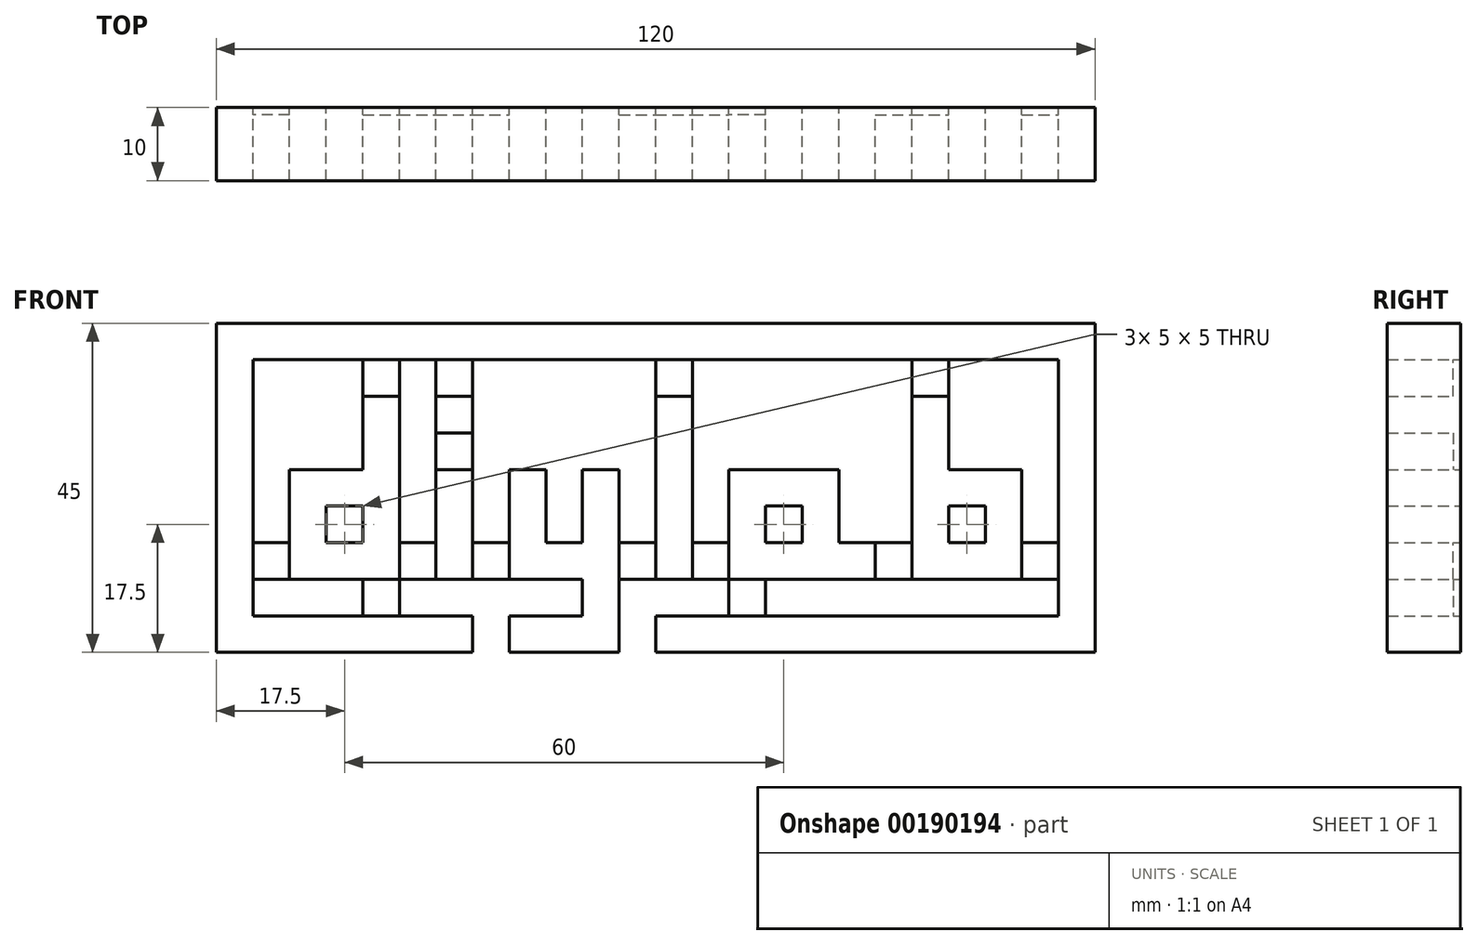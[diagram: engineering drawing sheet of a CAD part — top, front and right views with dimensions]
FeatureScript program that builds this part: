
annotation { "Feature Type Name" : "Feature", "Feature Type Description" : "" }
export const myFeature = defineFeature(function(context is Context, id is Id, definition is map)
    precondition{}
    {
        {
            var Q0;
            Q0=qCreatedBy(makeId("Front.planeOp"),FACE);
            var sketch = newSketch(context, id + "F0", { "sketchPlane" : qUnion([Q0])});
            skLineSegment(sketch, "E0", {"start": v(35, 0) * mm, "end": v(35, 5) * mm});
            skLineSegment(sketch, "E1", {"start": v(35, 5) * mm, "end": v(5, 5) * mm});
            skLineSegment(sketch, "E2", {"start": v(5, 5) * mm, "end": v(5, 40) * mm});
            skLineSegment(sketch, "E3", {"start": v(5, 40) * mm, "end": v(115, 40) * mm});
            skLineSegment(sketch, "E4", {"start": v(115, 40) * mm, "end": v(115, 5) * mm});
            skLineSegment(sketch, "E5", {"start": v(115, 5) * mm, "end": v(60, 5) * mm});
            skLineSegment(sketch, "E6", {"start": v(60, 5) * mm, "end": v(60, 0) * mm});
            skLineSegment(sketch, "E7", {"start": v(60, 0) * mm, "end": v(120, 0) * mm});
            skLineSegment(sketch, "E8", {"start": v(120, 0) * mm, "end": v(120, 45) * mm});
            skLineSegment(sketch, "E9", {"start": v(120, 45) * mm, "end": v(0, 45) * mm});
            skLineSegment(sketch, "E10", {"start": v(0, 45) * mm, "end": v(0, 0) * mm});
            skLineSegment(sketch, "E11", {"start": v(0, 0) * mm, "end": v(35, 0) * mm});
            skLineSegment(sketch, "E12", {"start": v(10, 25) * mm, "end": v(10, 10) * mm});
            skLineSegment(sketch, "E13", {"start": v(10, 10) * mm, "end": v(25, 10) * mm});
            skLineSegment(sketch, "E14", {"start": v(25, 10) * mm, "end": v(25, 35) * mm});
            skLineSegment(sketch, "E15", {"start": v(25, 35) * mm, "end": v(20, 35) * mm});
            skLineSegment(sketch, "E16", {"start": v(20, 35) * mm, "end": v(20, 25) * mm});
            skLineSegment(sketch, "E17", {"start": v(20, 25) * mm, "end": v(10, 25) * mm});
            skLineSegment(sketch, "E18", {"start": v(30, 25) * mm, "end": v(30, 10) * mm});
            skLineSegment(sketch, "E19", {"start": v(30, 10) * mm, "end": v(35, 10) * mm});
            skLineSegment(sketch, "E20", {"start": v(35, 10) * mm, "end": v(35, 25) * mm});
            skLineSegment(sketch, "E21", {"start": v(35, 25) * mm, "end": v(30, 25) * mm});
            skLineSegment(sketch, "E22", {"start": v(40, 5) * mm, "end": v(40, 0) * mm});
            skLineSegment(sketch, "E23", {"start": v(40, 0) * mm, "end": v(55, 0) * mm});
            skLineSegment(sketch, "E24", {"start": v(55, 0) * mm, "end": v(55, 25) * mm});
            skLineSegment(sketch, "E25", {"start": v(55, 25) * mm, "end": v(50, 25) * mm});
            skLineSegment(sketch, "E26", {"start": v(50, 25) * mm, "end": v(50, 15) * mm});
            skLineSegment(sketch, "E27", {"start": v(50, 15) * mm, "end": v(45, 15) * mm});
            skLineSegment(sketch, "E28", {"start": v(45, 15) * mm, "end": v(45, 25) * mm});
            skLineSegment(sketch, "E29", {"start": v(45, 25) * mm, "end": v(40, 25) * mm});
            skLineSegment(sketch, "E30", {"start": v(40, 25) * mm, "end": v(40, 10) * mm});
            skLineSegment(sketch, "E31", {"start": v(40, 10) * mm, "end": v(50, 10) * mm});
            skLineSegment(sketch, "E32", {"start": v(50, 10) * mm, "end": v(50, 5) * mm});
            skLineSegment(sketch, "E33", {"start": v(50, 5) * mm, "end": v(40, 5) * mm});
            skLineSegment(sketch, "E34", {"start": v(20, 15) * mm, "end": v(15, 15) * mm});
            skLineSegment(sketch, "E35", {"start": v(15, 15) * mm, "end": v(15, 20) * mm});
            skLineSegment(sketch, "E36", {"start": v(15, 20) * mm, "end": v(20, 20) * mm});
            skLineSegment(sketch, "E37", {"start": v(20, 20) * mm, "end": v(20, 15) * mm});
            skLineSegment(sketch, "E38", {"start": v(60, 35) * mm, "end": v(60, 10) * mm});
            skLineSegment(sketch, "E39", {"start": v(60, 10) * mm, "end": v(65, 10) * mm});
            skLineSegment(sketch, "E40", {"start": v(65, 10) * mm, "end": v(65, 35) * mm});
            skLineSegment(sketch, "E41", {"start": v(65, 35) * mm, "end": v(60, 35) * mm});
            skLineSegment(sketch, "E42", {"start": v(70, 10) * mm, "end": v(90, 10) * mm});
            skLineSegment(sketch, "E43", {"start": v(90, 10) * mm, "end": v(90, 15) * mm});
            skLineSegment(sketch, "E44", {"start": v(90, 15) * mm, "end": v(85, 15) * mm});
            skLineSegment(sketch, "E45", {"start": v(85, 15) * mm, "end": v(85, 25) * mm});
            skLineSegment(sketch, "E46", {"start": v(85, 25) * mm, "end": v(70, 25) * mm});
            skLineSegment(sketch, "E47", {"start": v(70, 25) * mm, "end": v(70, 10) * mm});
            skLineSegment(sketch, "E48", {"start": v(95, 10) * mm, "end": v(95, 35) * mm});
            skLineSegment(sketch, "E49", {"start": v(95, 35) * mm, "end": v(100, 35) * mm});
            skLineSegment(sketch, "E50", {"start": v(100, 35) * mm, "end": v(100, 25) * mm});
            skLineSegment(sketch, "E51", {"start": v(100, 25) * mm, "end": v(110, 25) * mm});
            skLineSegment(sketch, "E52", {"start": v(110, 25) * mm, "end": v(110, 10) * mm});
            skLineSegment(sketch, "E53", {"start": v(110, 10) * mm, "end": v(95, 10) * mm});
            skLineSegment(sketch, "E54", {"start": v(100, 20) * mm, "end": v(105, 20) * mm});
            skLineSegment(sketch, "E55", {"start": v(105, 20) * mm, "end": v(105, 15) * mm});
            skLineSegment(sketch, "E56", {"start": v(105, 15) * mm, "end": v(100, 15) * mm});
            skLineSegment(sketch, "E57", {"start": v(100, 15) * mm, "end": v(100, 20) * mm});
            skPoint(sketch, "E58.oppositeSnap0", {"position": v(102.5, 15) * mm});
            skLineSegment(sketch, "E58.bottom", {"start": v(75, 20) * mm, "end": v(80, 20) * mm});
            skLineSegment(sketch, "E58.top", {"start": v(75, 15) * mm, "end": v(80, 15) * mm});
            skLineSegment(sketch, "E58.left", {"start": v(75, 20) * mm, "end": v(75, 15) * mm});
            skLineSegment(sketch, "E58.right", {"start": v(80, 20) * mm, "end": v(80, 15) * mm});
            skLineSegment(sketch, "E59.bottom", {"start": v(30, 30) * mm, "end": v(35, 30) * mm});
            skLineSegment(sketch, "E59.top", {"start": v(30, 35) * mm, "end": v(35, 35) * mm});
            skLineSegment(sketch, "E59.left", {"start": v(30, 30) * mm, "end": v(30, 35) * mm});
            skLineSegment(sketch, "E59.right", {"start": v(35, 30) * mm, "end": v(35, 35) * mm});
            skLineSegment(sketch, "E60", {"start": v(10, 10) * mm, "end": v(5, 10) * mm});
            skLineSegment(sketch, "E61", {"start": v(10, 15) * mm, "end": v(5, 15) * mm});
            skLineSegment(sketch, "E62", {"start": v(20, 35) * mm, "end": v(20, 40) * mm});
            skLineSegment(sketch, "E63", {"start": v(25, 35) * mm, "end": v(25, 40) * mm});
            skLineSegment(sketch, "E64", {"start": v(30, 35) * mm, "end": v(30, 40) * mm});
            skLineSegment(sketch, "E65", {"start": v(35, 35) * mm, "end": v(35, 40) * mm});
            skLineSegment(sketch, "E66", {"start": v(30, 30) * mm, "end": v(30, 25) * mm});
            skLineSegment(sketch, "E67", {"start": v(35, 30) * mm, "end": v(35, 25) * mm});
            skLineSegment(sketch, "E68", {"start": v(25, 10) * mm, "end": v(25, 5) * mm});
            skLineSegment(sketch, "E69", {"start": v(20, 10) * mm, "end": v(20, 5) * mm});
            skLineSegment(sketch, "E70", {"start": v(25, 10) * mm, "end": v(30, 10) * mm});
            skLineSegment(sketch, "E71", {"start": v(35, 10) * mm, "end": v(40, 10) * mm});
            skLineSegment(sketch, "E72", {"start": v(25, 15) * mm, "end": v(30, 15) * mm});
            skLineSegment(sketch, "E73", {"start": v(35, 15) * mm, "end": v(40, 15) * mm});
            skLineSegment(sketch, "E74", {"start": v(55, 15) * mm, "end": v(60, 15) * mm});
            skLineSegment(sketch, "E75", {"start": v(55, 10) * mm, "end": v(60, 10) * mm});
            skLineSegment(sketch, "E76", {"start": v(65, 10) * mm, "end": v(70, 10) * mm});
            skLineSegment(sketch, "E77", {"start": v(65, 15) * mm, "end": v(70, 15) * mm});
            skLineSegment(sketch, "E78", {"start": v(90, 10) * mm, "end": v(95, 10) * mm});
            skLineSegment(sketch, "E79", {"start": v(90, 15) * mm, "end": v(95, 15) * mm});
            skLineSegment(sketch, "E80", {"start": v(110, 10) * mm, "end": v(115, 10) * mm});
            skLineSegment(sketch, "E81", {"start": v(110, 15) * mm, "end": v(115, 15) * mm});
            skLineSegment(sketch, "E82", {"start": v(95, 35) * mm, "end": v(95, 40) * mm});
            skLineSegment(sketch, "E83", {"start": v(100, 35) * mm, "end": v(100, 40) * mm});
            skLineSegment(sketch, "E84", {"start": v(60, 35) * mm, "end": v(60, 40) * mm});
            skLineSegment(sketch, "E85", {"start": v(65, 35) * mm, "end": v(65, 40) * mm});
            skLineSegment(sketch, "E86", {"start": v(70, 10) * mm, "end": v(70, 5) * mm});
            skLineSegment(sketch, "E87", {"start": v(75, 10) * mm, "end": v(75, 5) * mm});
            skSolve(sketch);
        }
        {
            var Q0;
            Q0=makeQuery(id+"F0.imprint","IMPRINT",FACE,{"disambiguationData":[TD([[makeQuery(id+"F0.imprint","IMPRINT",EDGE,{"derivedFrom":sQuery(id+"F0.wireOp",EDGE,"E0")}),1.0]])]});
            var Q1;
            Q1=makeQuery(id+"F0.imprint","IMPRINT",FACE,{"disambiguationData":[TD([[makeQuery(id+"F0.imprint","IMPRINT",EDGE,{"derivedFrom":sQuery(id+"F0.wireOp",EDGE,"E12")}),1.0]])]});
            var Q2;
            Q2=makeQuery(id+"F0.imprint","IMPRINT",FACE,{"disambiguationData":[TD([[makeQuery(id+"F0.imprint","IMPRINT",EDGE,{"derivedFrom":sQuery(id+"F0.wireOp",EDGE,"E59.bottom")}),1.0]])]});
            var Q3;
            Q3=makeQuery(id+"F0.imprint","IMPRINT",FACE,{"disambiguationData":[TD([[makeQuery(id+"F0.imprint","IMPRINT",EDGE,{"derivedFrom":sQuery(id+"F0.wireOp",EDGE,"E18")}),1.0]])]});
            var Q4;
            Q4=makeQuery(id+"F0.imprint","IMPRINT",FACE,{"disambiguationData":[TD([[makeQuery(id+"F0.imprint","IMPRINT",EDGE,{"derivedFrom":sQuery(id+"F0.wireOp",EDGE,"E22")}),1.0]])]});
            var Q5;
            Q5=makeQuery(id+"F0.imprint","IMPRINT",FACE,{"disambiguationData":[TD([[makeQuery(id+"F0.imprint","IMPRINT",EDGE,{"derivedFrom":sQuery(id+"F0.wireOp",EDGE,"E38")}),1.0]])]});
            var Q6;
            Q6=makeQuery(id+"F0.imprint","IMPRINT",FACE,{"disambiguationData":[TD([[makeQuery(id+"F0.imprint","IMPRINT",EDGE,{"derivedFrom":sQuery(id+"F0.wireOp",EDGE,"E42")}),1.0]])]});
            var Q7;
            Q7=makeQuery(id+"F0.imprint","IMPRINT",FACE,{"disambiguationData":[TD([[makeQuery(id+"F0.imprint","IMPRINT",EDGE,{"derivedFrom":sQuery(id+"F0.wireOp",EDGE,"E48")}),-1.0]])]});
            extrude(context, id + "F1", {"entities" : qUnion([Q0, Q1, Q2, Q3, Q4, Q5, Q6, Q7]), "depth" : 10 * mm});
        }
        {
            var Q0;
            Q0=makeQuery(id+"F0.imprint","IMPRINT",FACE,{"disambiguationData":[TD([[makeQuery(id+"F0.imprint","IMPRINT",EDGE,{"derivedFrom":sQuery(id+"F0.wireOp",EDGE,"E15")}),-1.0]])]});
            var Q1;
            Q1=makeQuery(id+"F0.imprint","IMPRINT",FACE,{"disambiguationData":[TD([[makeQuery(id+"F0.imprint","IMPRINT",EDGE,{"derivedFrom":sQuery(id+"F0.wireOp",EDGE,"E59.top")}),1.0]])]});
            var Q2;
            Q2=makeQuery(id+"F0.imprint","IMPRINT",FACE,{"disambiguationData":[TD([[makeQuery(id+"F0.imprint","IMPRINT",EDGE,{"derivedFrom":sQuery(id+"F0.wireOp",EDGE,"E21")}),-1.0]])]});
            var Q3;
            {var subQ0=sQuery(id+"F0.wireOp",EDGE,"E70");Q3=makeQuery(id+"F0.imprint","IMPRINT",FACE,{"disambiguationData":[TD([[makeQuery(id+"F0.imprint","IMPRINT",EDGE,{"derivedFrom":subQ0}),1.0]])]});}
            var Q4;
            {var subQ0=sQuery(id+"F0.wireOp",EDGE,"E68");Q4=makeQuery(id+"F0.imprint","IMPRINT",FACE,{"disambiguationData":[TD([[makeQuery(id+"F0.imprint","IMPRINT",EDGE,{"derivedFrom":subQ0}),-1.0]])]});}
            var Q5;
            {var subQ0=sQuery(id+"F0.wireOp",EDGE,"E60");Q5=makeQuery(id+"F0.imprint","IMPRINT",FACE,{"disambiguationData":[TD([[makeQuery(id+"F0.imprint","IMPRINT",EDGE,{"derivedFrom":subQ0}),-1.0]])]});}
            var Q6;
            {var subQ0=sQuery(id+"F0.wireOp",EDGE,"E71");Q6=makeQuery(id+"F0.imprint","IMPRINT",FACE,{"disambiguationData":[TD([[makeQuery(id+"F0.imprint","IMPRINT",EDGE,{"derivedFrom":subQ0}),1.0]])]});}
            var Q7;
            Q7=makeQuery(id+"F0.imprint","IMPRINT",FACE,{"disambiguationData":[TD([[makeQuery(id+"F0.imprint","IMPRINT",EDGE,{"derivedFrom":sQuery(id+"F0.wireOp",EDGE,"E41")}),-1.0]])]});
            var Q8;
            Q8=makeQuery(id+"F0.imprint","IMPRINT",FACE,{"disambiguationData":[TD([[makeQuery(id+"F0.imprint","IMPRINT",EDGE,{"derivedFrom":sQuery(id+"F0.wireOp",EDGE,"E49")}),1.0]])]});
            var Q9;
            {var subQ0=sQuery(id+"F0.wireOp",EDGE,"E74");Q9=makeQuery(id+"F0.imprint","IMPRINT",FACE,{"disambiguationData":[TD([[makeQuery(id+"F0.imprint","IMPRINT",EDGE,{"derivedFrom":subQ0}),-1.0]])]});}
            var Q10;
            {var subQ0=sQuery(id+"F0.wireOp",EDGE,"E76");Q10=makeQuery(id+"F0.imprint","IMPRINT",FACE,{"disambiguationData":[TD([[makeQuery(id+"F0.imprint","IMPRINT",EDGE,{"derivedFrom":subQ0}),1.0]])]});}
            var Q11;
            Q11=makeQuery(id+"F0.imprint","IMPRINT",FACE,{"disambiguationData":[TD([[makeQuery(id+"F0.imprint","IMPRINT",EDGE,{"derivedFrom":sQuery(id+"F0.wireOp",EDGE,"E43")}),-1.0]])]});
            var Q12;
            {var subQ0=sQuery(id+"F0.wireOp",EDGE,"E80");Q12=makeQuery(id+"F0.imprint","IMPRINT",FACE,{"disambiguationData":[TD([[makeQuery(id+"F0.imprint","IMPRINT",EDGE,{"derivedFrom":subQ0}),1.0]])]});}
            var Q13;
            {var subQ0=sQuery(id+"F0.wireOp",EDGE,"E86");Q13=makeQuery(id+"F0.imprint","IMPRINT",FACE,{"disambiguationData":[TD([[makeQuery(id+"F0.imprint","IMPRINT",EDGE,{"derivedFrom":subQ0}),1.0]])]});}
            extrude(context, id + "F2", {"entities" : qUnion([Q0, Q1, Q2, Q3, Q4, Q5, Q6, Q7, Q8, Q9, Q10, Q11, Q12, Q13]), "operationType" : NewBodyOperationType.ADD, "depth" : 1 * mm});
        }
    });
